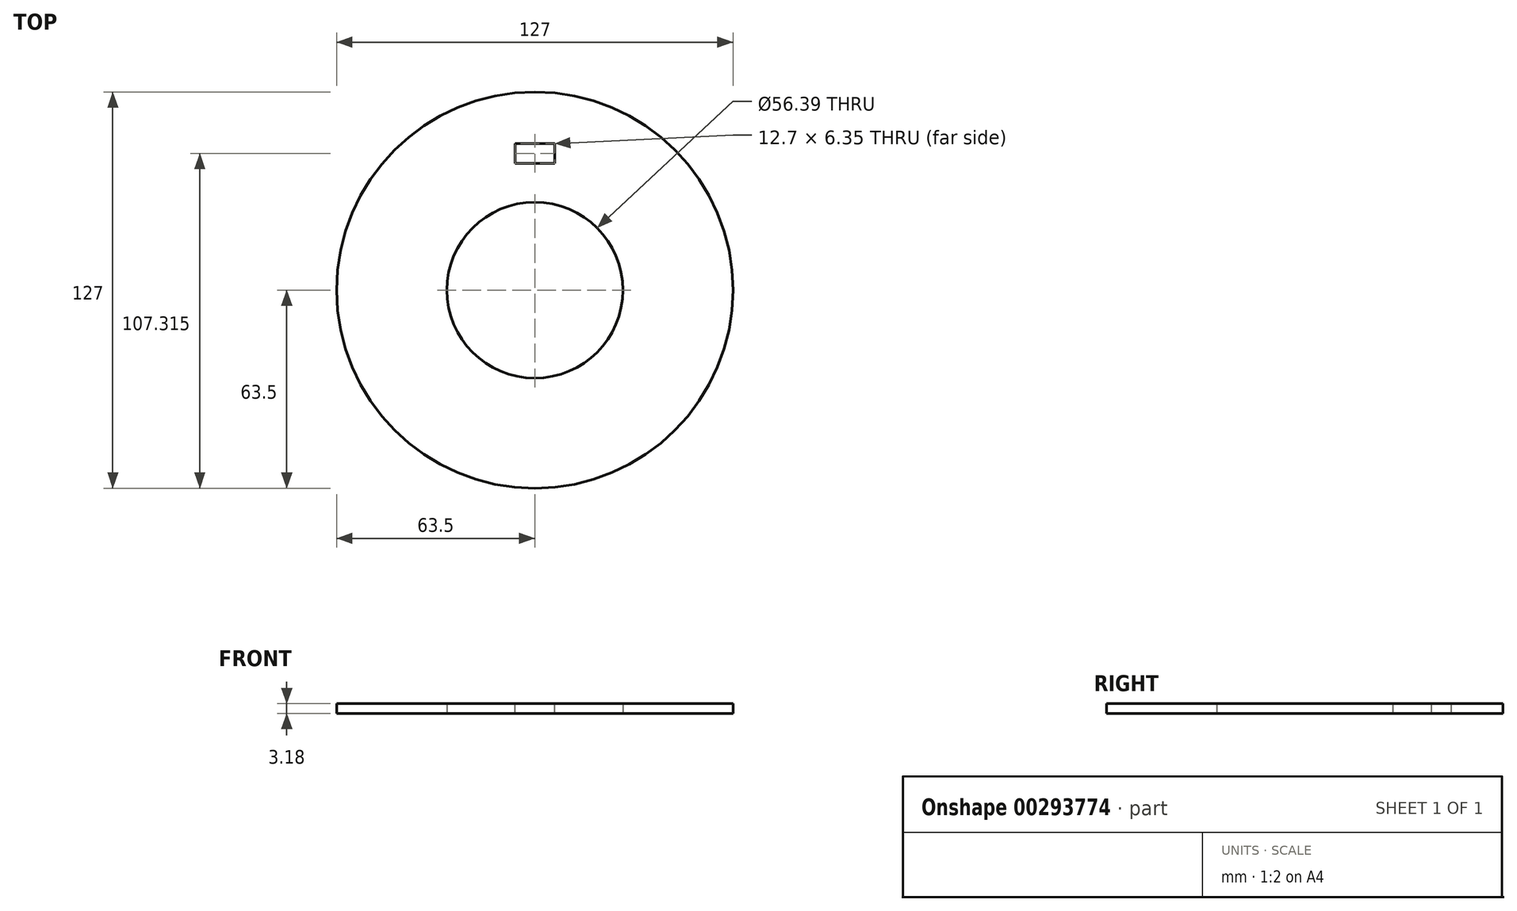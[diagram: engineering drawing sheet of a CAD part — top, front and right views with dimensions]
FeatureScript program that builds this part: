
annotation { "Feature Type Name" : "Feature", "Feature Type Description" : "" }
export const myFeature = defineFeature(function(context is Context, id is Id, definition is map)
    precondition{}
    {
        {
            var Q0;
            Q0=qCreatedBy(makeId("Top.planeOp"),FACE);
            var sketch = newSketch(context, id + "F0", { "sketchPlane" : qUnion([Q0])});
            skCircle(sketch, "E0", {"center": v(0, 0) * mm, "radius": 28.2 * mm});
            skCircle(sketch, "E1", {"center": v(0, 0) * mm, "radius": 63.5 * mm});
            skSolve(sketch);
        }
        {
            var Q0;
            Q0=makeQuery(id+"F0.imprint","IMPRINT",FACE,{"disambiguationData":[TD([[makeQuery(id+"F0.imprint","IMPRINT",EDGE,{"derivedFrom":sQuery(id+"F0.wireOp",EDGE,"E0")}),-1.0]])]});
            extrude(context, id + "F1", {"entities" : qUnion([Q0]), "depth" : 3.17 * mm});
        }
        {
            var Q0;
            Q0=makeQuery(id+"F1.opExtrude","CAP_FACE",FACE,{"disambiguationData":[OSD([sQuery(id+"F0.wireOp",EDGE,"E0"),sQuery(id+"F0.wireOp",EDGE,"E1")])],"isStart":false});
            var sketch = newSketch(context, id + "F2", { "sketchPlane" : qUnion([Q0])});
            skLineSegment(sketch, "E2.bottom", {"start": v(6.35, 47) * mm, "end": v(-6.35, 47) * mm});
            skLineSegment(sketch, "E2.top", {"start": v(6.35, 40.64) * mm, "end": v(-6.35, 40.64) * mm});
            skLineSegment(sketch, "E2.left", {"start": v(6.35, 47) * mm, "end": v(6.35, 40.64) * mm});
            skLineSegment(sketch, "E2.right", {"start": v(-6.35, 47) * mm, "end": v(-6.35, 40.64) * mm});
            skPoint(sketch, "E2.middle", {"position": v(0, 43.82) * mm});
            skCircle(sketch, "E3", {"center": v(0, 0) * mm, "radius": 50.8 * mm, "construction": true});
            skLineSegment(sketch, "E4.bottom", {"start": v(12.7, 47) * mm, "end": v(-12.7, 47) * mm, "construction": true});
            skLineSegment(sketch, "E4.top", {"start": v(12.7, 40.64) * mm, "end": v(-12.7, 40.64) * mm, "construction": true});
            skLineSegment(sketch, "E4.left", {"start": v(12.7, 47) * mm, "end": v(12.7, 40.64) * mm, "construction": true});
            skLineSegment(sketch, "E4.right", {"start": v(-12.7, 47) * mm, "end": v(-12.7, 40.64) * mm, "construction": true});
            skSolve(sketch);
        }
        {
            var Q0;
            Q0 = qSketchRegion(id + "F2", true);
            extrude(context, id + "F3", {"entities" : qUnion([Q0]), "operationType" : NewBodyOperationType.REMOVE, "endBound" : BoundingType.THROUGH_ALL, "oppositeDirection" : true, "depth" : 25.4 * mm});
        }
    });
